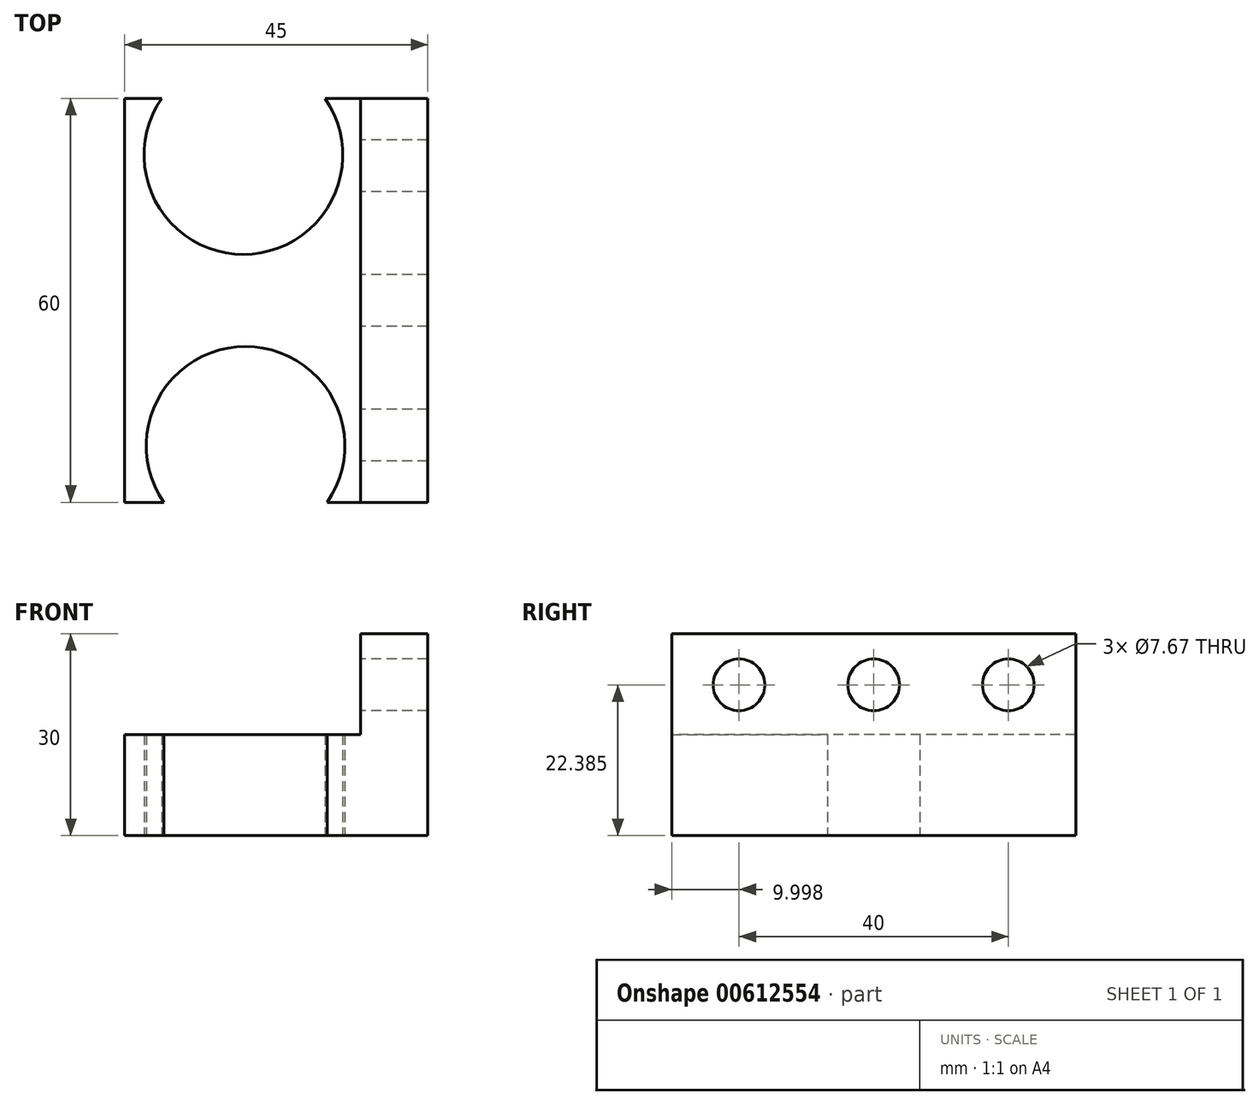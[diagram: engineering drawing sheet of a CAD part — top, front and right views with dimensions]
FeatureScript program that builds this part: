
annotation { "Feature Type Name" : "Feature", "Feature Type Description" : "" }
export const myFeature = defineFeature(function(context is Context, id is Id, definition is map)
    precondition{}
    {
        {
            var Q0;
            Q0=qCreatedBy(makeId("Top.planeOp"),FACE);
            var sketch = newSketch(context, id + "F0", { "sketchPlane" : qUnion([Q0])});
            skLineSegment(sketch, "E0.bottom", {"start": v(0, 0) * mm, "end": v(5.51, 0) * mm});
            skLineSegment(sketch, "E0.top", {"start": v(0, -60) * mm, "end": v(5.82, -60) * mm});
            skLineSegment(sketch, "E0.left", {"start": v(0, 0) * mm, "end": v(0, -60) * mm});
            skLineSegment(sketch, "E0.right", {"start": v(35, 0) * mm, "end": v(35, -60) * mm});
            skArc(sketch, "E1", {"start": v(5.51, 0) * mm, "mid": v(17.62, -23.17) * mm, "end": v(29.74, 0) * mm});
            skArc(sketch, "E2", {"start": v(30.07, -60) * mm, "mid": v(17.94, -36.85) * mm, "end": v(5.82, -60) * mm});
            skLineSegment(sketch, "E3.trimOffspring", {"start": v(29.74, 0) * mm, "end": v(35, 0) * mm});
            skLineSegment(sketch, "E4.trimOffspring", {"start": v(30.07, -60) * mm, "end": v(35, -60) * mm});
            skSolve(sketch);
        }
        {
            var Q0;
            Q0 = qSketchRegion(id + "F0", true);
            extrude(context, id + "F1", {"entities" : qUnion([Q0]), "depth" : 15 * mm, "offsetDistance" : 25 * mm});
        }
        {
            var Q0;
            Q0=makeQuery(id+"F1.opExtrude","SWEPT_FACE",FACE,{"disambiguationData":[OSD([sQuery(id+"F0.wireOp",EDGE,"E0.right")])]});
            var sketch = newSketch(context, id + "F2", { "sketchPlane" : qUnion([Q0])});
            skLineSegment(sketch, "E5.bottom", {"start": v(0, 0) * mm, "end": v(-60, 0) * mm});
            skLineSegment(sketch, "E5.top", {"start": v(0, 30) * mm, "end": v(-60, 30) * mm});
            skLineSegment(sketch, "E5.left", {"start": v(0, 0) * mm, "end": v(0, 30) * mm});
            skLineSegment(sketch, "E5.right", {"start": v(-60, 0) * mm, "end": v(-60, 30) * mm});
            skSolve(sketch);
        }
        {
            var Q0;
            Q0 = qSketchRegion(id + "F2", true);
            extrude(context, id + "F3", {"entities" : qUnion([Q0]), "operationType" : NewBodyOperationType.ADD, "depth" : 10 * mm, "offsetDistance" : 25 * mm});
        }
        {
            var Q0;
            Q0=makeQuery(id+"F3.opExtrude","CAP_FACE",FACE,{"disambiguationData":[OSD([sQuery(id+"F2.wireOp",EDGE,"E5.bottom"),sQuery(id+"F2.wireOp",EDGE,"E5.top"),sQuery(id+"F2.wireOp",EDGE,"E5.left"),sQuery(id+"F2.wireOp",EDGE,"E5.right")])],"isStart":true});
            var sketch = newSketch(context, id + "F4", { "sketchPlane" : qUnion([Q0])});
            skCircle(sketch, "E6", {"center": v(10, 22.38) * mm, "radius": 3.84 * mm});
            skCircle(sketch, "E7.1.0.0", {"center": v(30, 22.38) * mm, "radius": 3.84 * mm});
            skCircle(sketch, "E7.2.0.0", {"center": v(50, 22.38) * mm, "radius": 3.84 * mm});
            skLineSegment(sketch, "E7.direction1", {"start": v(10, 22.38) * mm, "end": v(30, 22.38) * mm, "construction": true});
            skSolve(sketch);
        }
        {
            var Q0;
            Q0 = qSketchRegion(id + "F4", true);
            extrude(context, id + "F5", {"entities" : qUnion([Q0]), "operationType" : NewBodyOperationType.REMOVE, "oppositeDirection" : true, "depth" : 25 * mm, "offsetDistance" : 25 * mm});
        }
    });
